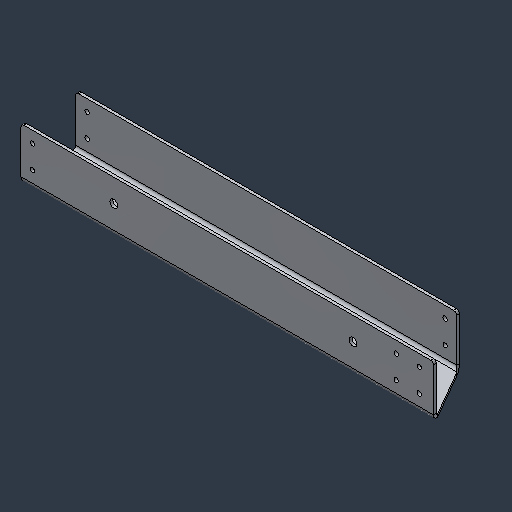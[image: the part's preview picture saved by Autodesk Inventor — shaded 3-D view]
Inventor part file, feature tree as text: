
AUTODESK INVENTOR PART (.ipt)
format: ipt  version: 2024.3 (Build 283343000, 343)  size: 131,072 bytes
history: native  units: mm (DEFAULTED — no unit token found)
features: fillet x1
ambient origin geometry x8: Origin, YZ Plane, XZ Plane, XY Plane, X Axis, Y Axis, Z Axis, Center Point
bodies: Solid1 (feature_tree)
feature tree (1):
  fillet  "Fillet1"  [1 undecoded]
note: 1 required parameter value undecoded (feature->parameter linkage not recoverable at this tier; creation-order binding heuristic only, values carry confidence <= 0.55)
